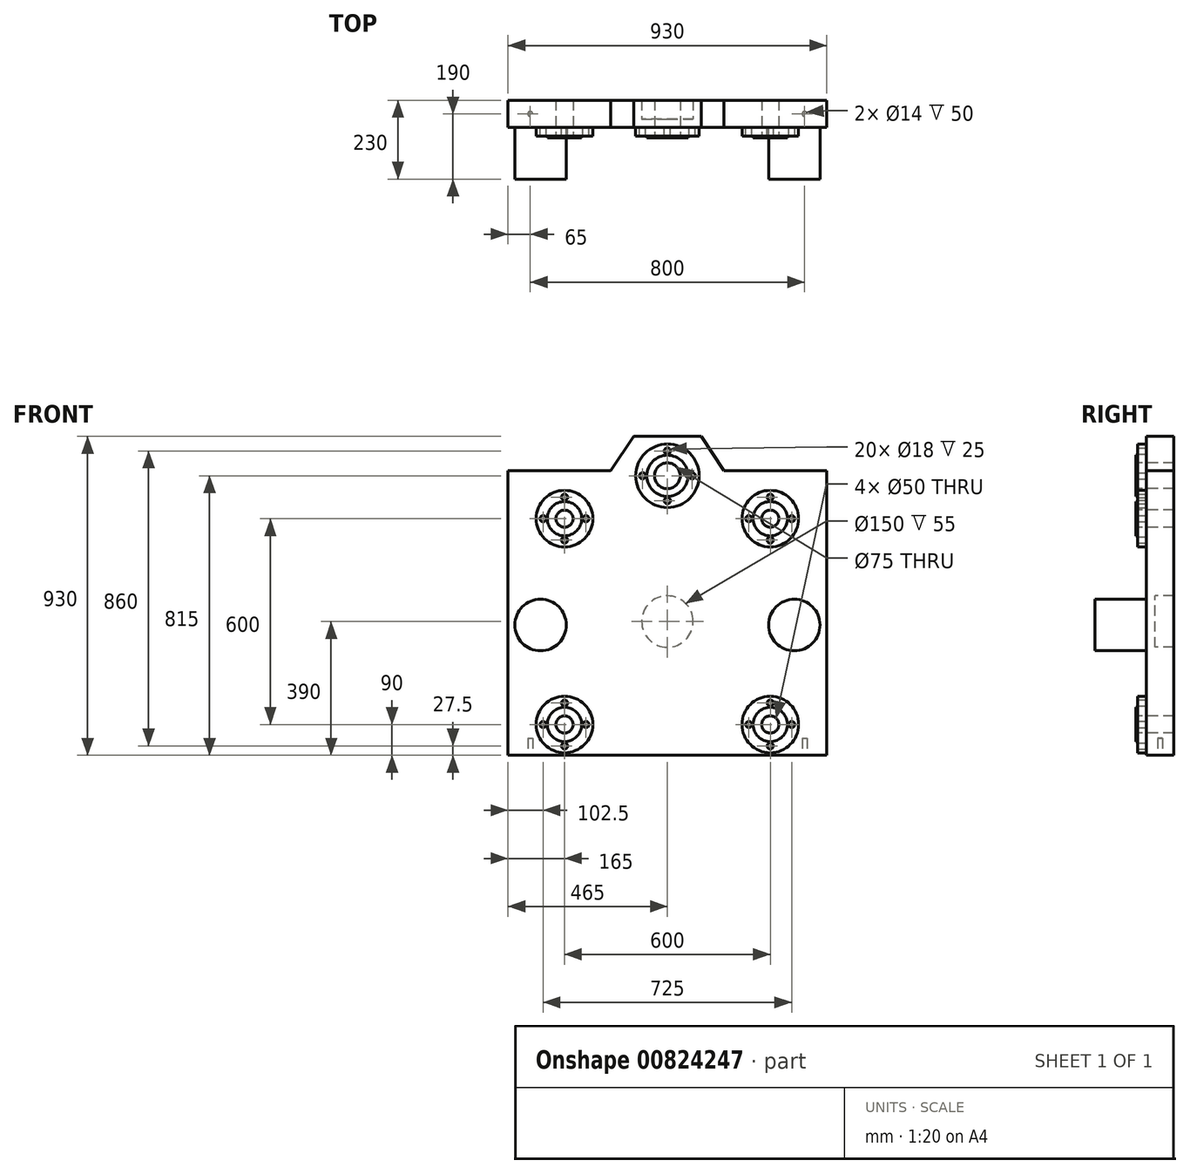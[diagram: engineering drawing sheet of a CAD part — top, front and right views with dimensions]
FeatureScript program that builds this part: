
annotation { "Feature Type Name" : "Feature", "Feature Type Description" : "" }
export const myFeature = defineFeature(function(context is Context, id is Id, definition is map)
    precondition{}
    {
        {
            var Q0;
            Q0=qCreatedBy(makeId("Front.planeOp"),FACE);
            var sketch = newSketch(context, id + "F0", { "sketchPlane" : qUnion([Q0])});
            skLineSegment(sketch, "E0.bottom", {"start": v(465, -965) * mm, "end": v(345, -965) * mm});
            skLineSegment(sketch, "E0.top", {"start": v(465, 965) * mm, "end": v(-465, 965) * mm});
            skLineSegment(sketch, "E0.left", {"start": v(465, -965) * mm, "end": v(465, 965) * mm});
            skLineSegment(sketch, "E0.right", {"start": v(-465, -965) * mm, "end": v(-465, 965) * mm});
            skPoint(sketch, "E0.middle", {"position": v(0, 0) * mm});
            skLineSegment(sketch, "E1.top", {"start": v(-345, -765) * mm, "end": v(345, -765) * mm});
            skLineSegment(sketch, "E1.left", {"start": v(-345, -965) * mm, "end": v(-345, -765) * mm});
            skLineSegment(sketch, "E1.right", {"start": v(345, -965) * mm, "end": v(345, -765) * mm});
            skLineSegment(sketch, "E2.bottom", {"start": v(-345, -645) * mm, "end": v(345, -645) * mm});
            skLineSegment(sketch, "E2.top", {"start": v(-345, -295) * mm, "end": v(345, -295) * mm});
            skLineSegment(sketch, "E2.left", {"start": v(-345, -645) * mm, "end": v(-345, -295) * mm});
            skLineSegment(sketch, "E2.right", {"start": v(345, -645) * mm, "end": v(345, -295) * mm});
            skLineSegment(sketch, "E3.trimOffspring", {"start": v(-345, -965) * mm, "end": v(-465, -965) * mm});
            skLineSegment(sketch, "E4.bottom", {"start": v(-345, -175) * mm, "end": v(345, -175) * mm});
            skLineSegment(sketch, "E4.top", {"start": v(-345, 25) * mm, "end": v(345, 25) * mm});
            skLineSegment(sketch, "E4.left", {"start": v(-345, -175) * mm, "end": v(-345, 25) * mm});
            skLineSegment(sketch, "E4.right", {"start": v(345, -175) * mm, "end": v(345, 25) * mm});
            skPoint(sketch, "E5.middle", {"position": v(0, 425) * mm});
            skSolve(sketch);
        }
        {
            var Q0;
            Q0=makeQuery(id+"F0.imprint","IMPRINT",FACE,{"disambiguationData":[TD([[makeQuery(id+"F0.imprint","IMPRINT",EDGE,{"derivedFrom":sQuery(id+"F0.wireOp",EDGE,"E0.bottom")}),-1.0]])]});
            extrude(context, id + "F1", {"entities" : qUnion([Q0]), "depth" : 80 * mm, "offsetDistance" : 25 * mm});
        }
        {
            var Q0;
            Q0=makeQuery(id+"F1.opExtrude","CAP_FACE",FACE,{"disambiguationData":[OSD([sQuery(id+"F0.wireOp",EDGE,"E0.bottom"),sQuery(id+"F0.wireOp",EDGE,"E0.top"),sQuery(id+"F0.wireOp",EDGE,"E0.left"),sQuery(id+"F0.wireOp",EDGE,"E0.right"),sQuery(id+"F0.wireOp",EDGE,"E1.top"),sQuery(id+"F0.wireOp",EDGE,"E1.left"),sQuery(id+"F0.wireOp",EDGE,"E1.right"),sQuery(id+"F0.wireOp",EDGE,"E2.bottom"),sQuery(id+"F0.wireOp",EDGE,"E2.top"),sQuery(id+"F0.wireOp",EDGE,"E2.left"),sQuery(id+"F0.wireOp",EDGE,"E2.right"),sQuery(id+"F0.wireOp",EDGE,"E3.trimOffspring"),sQuery(id+"F0.wireOp",EDGE,"nSGubIzk-R7de-6MO4-penA-cvBglKJnvsGC"),sQuery(id+"F0.wireOp",EDGE,"E4.bottom"),sQuery(id+"F0.wireOp",EDGE,"E4.top"),sQuery(id+"F0.wireOp",EDGE,"E4.left"),sQuery(id+"F0.wireOp",EDGE,"E4.right")])],"isStart":false});
            var sketch = newSketch(context, id + "F2", { "sketchPlane" : qUnion([Q0])});
            skCircle(sketch, "E6", {"center": v(-300, 125) * mm, "radius": 25 * mm});
            skCircle(sketch, "E7.0", {"center": v(0, 425) * mm, "radius": 75 * mm});
            skCircle(sketch, "E8.0.1.0", {"center": v(-300, 725) * mm, "radius": 25 * mm});
            skCircle(sketch, "E8.1.0.0", {"center": v(300, 125) * mm, "radius": 25 * mm});
            skCircle(sketch, "E8.1.1.0", {"center": v(300, 725) * mm, "radius": 25 * mm});
            skLineSegment(sketch, "E8.direction1", {"start": v(-300, 125) * mm, "end": v(300, 125) * mm, "construction": true});
            skLineSegment(sketch, "E8.direction2", {"start": v(-300, 125) * mm, "end": v(-300, 725) * mm, "construction": true});
            skSolve(sketch);
        }
        {
            var Q0;
            Q0=qSketchRegion(id+"F2",true);
            extrude(context, id + "F3", {"entities" : qUnion([Q0]), "operationType" : NewBodyOperationType.REMOVE, "oppositeDirection" : true, "depth" : 100 * mm, "offsetDistance" : 25 * mm});
        }
        {
            var Q0;
            Q0=makeQuery(id+"F1.opExtrude","CAP_FACE",FACE,{"disambiguationData":[OSD([sQuery(id+"F0.wireOp",EDGE,"E0.bottom"),sQuery(id+"F0.wireOp",EDGE,"E0.top"),sQuery(id+"F0.wireOp",EDGE,"E0.left"),sQuery(id+"F0.wireOp",EDGE,"E0.right"),sQuery(id+"F0.wireOp",EDGE,"E1.top"),sQuery(id+"F0.wireOp",EDGE,"E1.left"),sQuery(id+"F0.wireOp",EDGE,"E1.right"),sQuery(id+"F0.wireOp",EDGE,"E2.bottom"),sQuery(id+"F0.wireOp",EDGE,"E2.top"),sQuery(id+"F0.wireOp",EDGE,"E2.left"),sQuery(id+"F0.wireOp",EDGE,"E2.right"),sQuery(id+"F0.wireOp",EDGE,"E3.trimOffspring"),sQuery(id+"F0.wireOp",EDGE,"nSGubIzk-R7de-6MO4-penA-cvBglKJnvsGC"),sQuery(id+"F0.wireOp",EDGE,"E4.bottom"),sQuery(id+"F0.wireOp",EDGE,"E4.top"),sQuery(id+"F0.wireOp",EDGE,"E4.left"),sQuery(id+"F0.wireOp",EDGE,"E4.right")])],"isStart":false});
            var sketch = newSketch(context, id + "F4", { "sketchPlane" : qUnion([Q0])});
            skCircle(sketch, "E9", {"center": v(-370, 415) * mm, "radius": 75 * mm});
            skCircle(sketch, "E10.MirrorC", {"center": v(370, 415) * mm, "radius": 75 * mm});
            skSolve(sketch);
        }
        {
            var Q0;
            Q0=qSketchRegion(id+"F4",true);
            extrude(context, id + "F5", {"entities" : qUnion([Q0]), "operationType" : NewBodyOperationType.ADD, "depth" : 150 * mm, "offsetDistance" : 25 * mm});
        }
        {
            var Q0;
            Q0=makeQuery(id+"F1.opExtrude","CAP_FACE",FACE,{"disambiguationData":[OSD([sQuery(id+"F0.wireOp",EDGE,"E0.bottom"),sQuery(id+"F0.wireOp",EDGE,"E0.top"),sQuery(id+"F0.wireOp",EDGE,"E0.left"),sQuery(id+"F0.wireOp",EDGE,"E0.right"),sQuery(id+"F0.wireOp",EDGE,"E1.top"),sQuery(id+"F0.wireOp",EDGE,"E1.left"),sQuery(id+"F0.wireOp",EDGE,"E1.right"),sQuery(id+"F0.wireOp",EDGE,"E2.bottom"),sQuery(id+"F0.wireOp",EDGE,"E2.top"),sQuery(id+"F0.wireOp",EDGE,"E2.left"),sQuery(id+"F0.wireOp",EDGE,"E2.right"),sQuery(id+"F0.wireOp",EDGE,"E3.trimOffspring"),sQuery(id+"F0.wireOp",EDGE,"nSGubIzk-R7de-6MO4-penA-cvBglKJnvsGC"),sQuery(id+"F0.wireOp",EDGE,"E4.bottom"),sQuery(id+"F0.wireOp",EDGE,"E4.top"),sQuery(id+"F0.wireOp",EDGE,"E4.left"),sQuery(id+"F0.wireOp",EDGE,"E4.right")])],"isStart":false});
            var sketch = newSketch(context, id + "F6", { "sketchPlane" : qUnion([Q0])});
            skCircle(sketch, "E11", {"center": v(-300, 725) * mm, "radius": 82.5 * mm});
            skCircle(sketch, "E12", {"center": v(-300, 787.5) * mm, "radius": 9 * mm});
            skCircle(sketch, "E13.0", {"center": v(-300, 725) * mm, "radius": 25 * mm});
            skCircle(sketch, "E14.1.0", {"center": v(-362.5, 725) * mm, "radius": 9 * mm});
            skCircle(sketch, "E14.2.0", {"center": v(-300, 662.5) * mm, "radius": 9 * mm});
            skCircle(sketch, "E14.3.0", {"center": v(-237.5, 725) * mm, "radius": 9 * mm});
            skPoint(sketch, "E15.0.1.0", {"position": v(-300, 125) * mm});
            skCircle(sketch, "E15.0.1.1", {"center": v(-300, 125) * mm, "radius": 82.5 * mm});
            skCircle(sketch, "E15.0.1.2", {"center": v(-300, 125) * mm, "radius": 25 * mm});
            skCircle(sketch, "E15.0.1.3", {"center": v(-237.5, 125) * mm, "radius": 9 * mm});
            skCircle(sketch, "E15.0.1.4", {"center": v(-362.5, 125) * mm, "radius": 9 * mm});
            skCircle(sketch, "E15.0.1.5", {"center": v(-300, 187.5) * mm, "radius": 9 * mm});
            skCircle(sketch, "E15.0.1.6", {"center": v(-300, 62.5) * mm, "radius": 9 * mm});
            skPoint(sketch, "E15.1.0.0", {"position": v(300, 725) * mm});
            skCircle(sketch, "E15.1.0.1", {"center": v(300, 725) * mm, "radius": 82.5 * mm});
            skCircle(sketch, "E15.1.0.2", {"center": v(300, 725) * mm, "radius": 25 * mm});
            skCircle(sketch, "E15.1.0.3", {"center": v(362.5, 725) * mm, "radius": 9 * mm});
            skCircle(sketch, "E15.1.0.4", {"center": v(237.5, 725) * mm, "radius": 9 * mm});
            skCircle(sketch, "E15.1.0.5", {"center": v(300, 787.5) * mm, "radius": 9 * mm});
            skCircle(sketch, "E15.1.0.6", {"center": v(300, 662.5) * mm, "radius": 9 * mm});
            skPoint(sketch, "E15.1.1.0", {"position": v(300, 125) * mm});
            skCircle(sketch, "E15.1.1.1", {"center": v(300, 125) * mm, "radius": 82.5 * mm});
            skCircle(sketch, "E15.1.1.2", {"center": v(300, 125) * mm, "radius": 25 * mm});
            skCircle(sketch, "E15.1.1.3", {"center": v(362.5, 125) * mm, "radius": 9 * mm});
            skCircle(sketch, "E15.1.1.4", {"center": v(237.5, 125) * mm, "radius": 9 * mm});
            skCircle(sketch, "E15.1.1.5", {"center": v(300, 187.5) * mm, "radius": 9 * mm});
            skCircle(sketch, "E15.1.1.6", {"center": v(300, 62.5) * mm, "radius": 9 * mm});
            skLineSegment(sketch, "E15.direction1", {"start": v(-300, 662.5) * mm, "end": v(300, 662.5) * mm, "construction": true});
            skLineSegment(sketch, "E15.direction2", {"start": v(-300, 662.5) * mm, "end": v(-300, 62.5) * mm, "construction": true});
            skSolve(sketch);
        }
        {
            var Q0;
            Q0=qSketchRegion(id+"F6",true);
            extrude(context, id + "F7", {"entities" : qUnion([Q0]), "operationType" : NewBodyOperationType.ADD, "depth" : 25 * mm, "offsetDistance" : 25 * mm});
        }
        {
            var Q0;
            Q0=makeQuery(id+"F7.opExtrude","CAP_FACE",FACE,{"disambiguationData":[OSD([sQuery(id+"F6.wireOp",EDGE,"E11"),sQuery(id+"F6.wireOp",EDGE,"E12"),sQuery(id+"F6.wireOp",EDGE,"E13.0"),sQuery(id+"F6.wireOp",EDGE,"E14.1.0"),sQuery(id+"F6.wireOp",EDGE,"E14.2.0"),sQuery(id+"F6.wireOp",EDGE,"E14.3.0")])],"isStart":false});
            var sketch = newSketch(context, id + "F8", { "sketchPlane" : qUnion([Q0])});
            skCircle(sketch, "E16", {"center": v(-300, 725) * mm, "radius": 50 * mm});
            skCircle(sketch, "E17.0.1.0", {"center": v(-300, 125) * mm, "radius": 50 * mm});
            skCircle(sketch, "E17.1.0.0", {"center": v(300, 725) * mm, "radius": 50 * mm});
            skCircle(sketch, "E17.1.1.0", {"center": v(300, 125) * mm, "radius": 50 * mm});
            skLineSegment(sketch, "E17.direction1", {"start": v(-300, 725) * mm, "end": v(300, 725) * mm, "construction": true});
            skLineSegment(sketch, "E17.direction2", {"start": v(-300, 725) * mm, "end": v(-300, 125) * mm, "construction": true});
            skCircle(sketch, "E18", {"center": v(300, 725) * mm, "radius": 25 * mm});
            skCircle(sketch, "E19", {"center": v(300, 125) * mm, "radius": 25 * mm});
            skCircle(sketch, "E20", {"center": v(-300, 125) * mm, "radius": 25 * mm});
            skCircle(sketch, "E21", {"center": v(-300, 725) * mm, "radius": 25 * mm});
            skSolve(sketch);
        }
        {
            var Q0;
            Q0=qSketchRegion(id+"F8",true);
            extrude(context, id + "F9", {"entities" : qUnion([Q0]), "operationType" : NewBodyOperationType.ADD, "depth" : 5 * mm, "offsetDistance" : 25 * mm});
        }
        {
            var Q0;
            {var subQ0=sQuery(id+"F0.wireOp",EDGE,"E4.right");var subQ1=sQuery(id+"F0.wireOp",EDGE,"E4.left");var subQ2=sQuery(id+"F0.wireOp",EDGE,"E4.top");var subQ3=sQuery(id+"F0.wireOp",EDGE,"E1.left");var subQ4=sQuery(id+"F0.wireOp",EDGE,"E4.bottom");var subQ5=sQuery(id+"F0.wireOp",EDGE,"E3.trimOffspring");var subQ6=sQuery(id+"F0.wireOp",EDGE,"E2.right");var subQ7=sQuery(id+"F0.wireOp",EDGE,"E0.left");var subQ8=sQuery(id+"F0.wireOp",EDGE,"E0.top");var subQ9=sQuery(id+"F0.wireOp",EDGE,"E0.right");var subQ10=sQuery(id+"F0.wireOp",EDGE,"E2.bottom");var subQ11=sQuery(id+"F0.wireOp",EDGE,"E0.bottom");var subQ12=sQuery(id+"F0.wireOp",EDGE,"E2.left");var subQ13=sQuery(id+"F0.wireOp",EDGE,"E1.top");var subQ14=sQuery(id+"F0.wireOp",EDGE,"E1.right");var subQ15=sQuery(id+"F0.wireOp",EDGE,"E2.top");Q0=makeQuery(id+"F7.boolean.opBoolean","SPLIT",FACE,{"disambiguationData":[TD([makeQuery(id+"F1.opExtrude","SWEPT_FACE",FACE,{"disambiguationData":[OSD([subQ11])]})])],"derivedFrom":makeQuery(id+"F1.opExtrude","CAP_FACE",FACE,{"disambiguationData":[OSD([subQ11,subQ8,subQ7,subQ9,subQ13,subQ3,subQ14,subQ10,subQ15,subQ12,subQ6,subQ5,subQ4,subQ2,subQ1,subQ0])],"isStart":false})});}
            var sketch = newSketch(context, id + "F10", { "sketchPlane" : qUnion([Q0])});
            skCircle(sketch, "E22.0", {"center": v(0, 425) * mm, "radius": 75 * mm});
            skSolve(sketch);
        }
        {
            var Q0;
            Q0=qSketchRegion(id+"F10",true);
            extrude(context, id + "F11", {"entities" : qUnion([Q0]), "operationType" : NewBodyOperationType.ADD, "oppositeDirection" : true, "depth" : 25 * mm, "offsetDistance" : 25 * mm});
        }
        {
            var Q0;
            {var subQ0=sQuery(id+"F0.wireOp",EDGE,"E4.right");var subQ1=sQuery(id+"F0.wireOp",EDGE,"E4.left");var subQ2=sQuery(id+"F0.wireOp",EDGE,"E4.top");var subQ3=sQuery(id+"F0.wireOp",EDGE,"E1.left");var subQ4=sQuery(id+"F0.wireOp",EDGE,"E4.bottom");var subQ5=sQuery(id+"F0.wireOp",EDGE,"E3.trimOffspring");var subQ6=sQuery(id+"F0.wireOp",EDGE,"E2.right");var subQ7=sQuery(id+"F0.wireOp",EDGE,"E0.left");var subQ8=sQuery(id+"F0.wireOp",EDGE,"E0.top");var subQ9=sQuery(id+"F0.wireOp",EDGE,"E0.right");var subQ10=sQuery(id+"F0.wireOp",EDGE,"E2.bottom");var subQ11=sQuery(id+"F0.wireOp",EDGE,"E0.bottom");var subQ12=sQuery(id+"F0.wireOp",EDGE,"E2.left");var subQ13=sQuery(id+"F0.wireOp",EDGE,"E1.top");var subQ14=sQuery(id+"F0.wireOp",EDGE,"E1.right");var subQ15=sQuery(id+"F0.wireOp",EDGE,"E2.top");Q0=makeQuery(id+"F11.boolean.opBoolean","MERGE",FACE,{"derivedFrom":[makeQuery(id+"F7.boolean.opBoolean","SPLIT",FACE,{"disambiguationData":[TD([makeQuery(id+"F1.opExtrude","SWEPT_FACE",FACE,{"disambiguationData":[OSD([subQ11])]})])],"derivedFrom":makeQuery(id+"F1.opExtrude","CAP_FACE",FACE,{"disambiguationData":[OSD([subQ11,subQ8,subQ7,subQ9,subQ13,subQ3,subQ14,subQ10,subQ15,subQ12,subQ6,subQ5,subQ4,subQ2,subQ1,subQ0])],"isStart":false})}),makeQuery(id+"F11.opExtrude","CAP_FACE",FACE,{"disambiguationData":[OSD([sQuery(id+"F10.wireOp",EDGE,"E22.0")])],"isStart":true})]});}
            var sketch = newSketch(context, id + "F12", { "sketchPlane" : qUnion([Q0])});
            skCircle(sketch, "E23", {"center": v(0, 850) * mm, "radius": 37.5 * mm});
            skPoint(sketch, "E23.centerSnap0", {"position": v(0, 965) * mm});
            skCircle(sketch, "E24.0", {"center": v(300, 725) * mm, "radius": 25 * mm});
            skSolve(sketch);
        }
        {
            var Q0;
            Q0=makeQuery(id+"F12.imprint","IMPRINT",FACE,{"disambiguationData":[TD([[makeQuery(id+"F12.imprint","IMPRINT",EDGE,{"derivedFrom":sQuery(id+"F12.wireOp",EDGE,"E23")}),1.0]])]});
            extrude(context, id + "F13", {"entities" : qUnion([Q0]), "operationType" : NewBodyOperationType.REMOVE, "oppositeDirection" : true, "depth" : 100 * mm, "offsetDistance" : 25 * mm});
        }
        {
            var Q0;
            {var subQ0=sQuery(id+"F0.wireOp",EDGE,"E4.right");var subQ1=sQuery(id+"F0.wireOp",EDGE,"E4.left");var subQ2=sQuery(id+"F0.wireOp",EDGE,"E4.top");var subQ3=sQuery(id+"F0.wireOp",EDGE,"E1.left");var subQ4=sQuery(id+"F0.wireOp",EDGE,"E4.bottom");var subQ5=sQuery(id+"F0.wireOp",EDGE,"E3.trimOffspring");var subQ6=sQuery(id+"F0.wireOp",EDGE,"E2.right");var subQ7=sQuery(id+"F0.wireOp",EDGE,"E0.left");var subQ8=sQuery(id+"F0.wireOp",EDGE,"E0.top");var subQ9=sQuery(id+"F0.wireOp",EDGE,"E0.right");var subQ10=sQuery(id+"F0.wireOp",EDGE,"E2.bottom");var subQ11=sQuery(id+"F0.wireOp",EDGE,"E0.bottom");var subQ12=sQuery(id+"F0.wireOp",EDGE,"E2.left");var subQ13=sQuery(id+"F0.wireOp",EDGE,"E1.top");var subQ14=sQuery(id+"F0.wireOp",EDGE,"E1.right");var subQ15=sQuery(id+"F0.wireOp",EDGE,"E2.top");Q0=makeQuery(id+"F11.boolean.opBoolean","MERGE",FACE,{"derivedFrom":[makeQuery(id+"F7.boolean.opBoolean","SPLIT",FACE,{"disambiguationData":[TD([makeQuery(id+"F1.opExtrude","SWEPT_FACE",FACE,{"disambiguationData":[OSD([subQ11])]})])],"derivedFrom":makeQuery(id+"F1.opExtrude","CAP_FACE",FACE,{"disambiguationData":[OSD([subQ11,subQ8,subQ7,subQ9,subQ13,subQ3,subQ14,subQ10,subQ15,subQ12,subQ6,subQ5,subQ4,subQ2,subQ1,subQ0])],"isStart":false})}),makeQuery(id+"F11.opExtrude","CAP_FACE",FACE,{"disambiguationData":[OSD([sQuery(id+"F10.wireOp",EDGE,"E22.0")])],"isStart":true})]});}
            var sketch = newSketch(context, id + "F14", { "sketchPlane" : qUnion([Q0])});
            skCircle(sketch, "E25", {"center": v(0, 850) * mm, "radius": 92.5 * mm});
            skCircle(sketch, "E26", {"center": v(0, 922.5) * mm, "radius": 9 * mm});
            skCircle(sketch, "E27.1.0", {"center": v(-72.5, 850) * mm, "radius": 9 * mm});
            skCircle(sketch, "E27.2.0", {"center": v(0, 777.5) * mm, "radius": 9 * mm});
            skCircle(sketch, "E27.3.0", {"center": v(72.5, 850) * mm, "radius": 9 * mm});
            skSolve(sketch);
        }
        {
            var Q0;
            Q0=makeQuery(id+"F14.imprint","IMPRINT",FACE,{"disambiguationData":[TD([[makeQuery(id+"F14.imprint","IMPRINT",EDGE,{"derivedFrom":sQuery(id+"F14.wireOp",EDGE,"E25")}),1.0]])]});
            extrude(context, id + "F15", {"entities" : qUnion([Q0]), "operationType" : NewBodyOperationType.ADD, "depth" : 25 * mm, "offsetDistance" : 25 * mm});
        }
        {
            var Q0;
            Q0=makeQuery(id+"F15.opExtrude","CAP_FACE",FACE,{"disambiguationData":[OSD([sQuery(id+"F12.wireOp",EDGE,"E23"),sQuery(id+"F14.wireOp",EDGE,"E25"),sQuery(id+"F14.wireOp",EDGE,"E26"),sQuery(id+"F14.wireOp",EDGE,"E27.1.0"),sQuery(id+"F14.wireOp",EDGE,"E27.2.0"),sQuery(id+"F14.wireOp",EDGE,"E27.3.0")])],"isStart":false});
            var sketch = newSketch(context, id + "F16", { "sketchPlane" : qUnion([Q0])});
            skCircle(sketch, "E28", {"center": v(0, 850) * mm, "radius": 60 * mm});
            skSolve(sketch);
        }
        {
            var Q0;
            Q0=makeQuery(id+"F16.imprint","IMPRINT",FACE,{"disambiguationData":[TD([[makeQuery(id+"F16.imprint","IMPRINT",EDGE,{"derivedFrom":sQuery(id+"F16.wireOp",EDGE,"E28")}),1.0]])]});
            extrude(context, id + "F17", {"entities" : qUnion([Q0]), "operationType" : NewBodyOperationType.ADD, "depth" : 5 * mm, "offsetDistance" : 25 * mm});
        }
        {
            var Q0;
            {var subQ2=sQuery(id+"F0.wireOp",EDGE,"E4.right");var subQ5=sQuery(id+"F0.wireOp",EDGE,"E4.left");var subQ8=sQuery(id+"F0.wireOp",EDGE,"E4.top");var subQ10=sQuery(id+"F0.wireOp",EDGE,"E4.bottom");var subQ12=sQuery(id+"F0.wireOp",EDGE,"E3.trimOffspring");var subQ14=sQuery(id+"F0.wireOp",EDGE,"E2.right");var subQ16=sQuery(id+"F0.wireOp",EDGE,"E0.left");var subQ18=sQuery(id+"F0.wireOp",EDGE,"E0.top");var subQ20=sQuery(id+"F0.wireOp",EDGE,"E0.right");var subQ23=sQuery(id+"F0.wireOp",EDGE,"E2.bottom");var subQ25=sQuery(id+"F0.wireOp",EDGE,"E0.bottom");var subQ26=makeQuery(id+"F1.opExtrude","SWEPT_FACE",FACE,{"disambiguationData":[OSD([subQ25])]});var subQ27=sQuery(id+"F0.wireOp",EDGE,"E2.left");var subQ29=sQuery(id+"F0.wireOp",EDGE,"E1.top");var subQ32=sQuery(id+"F0.wireOp",EDGE,"E1.left");var subQ34=sQuery(id+"F0.wireOp",EDGE,"E1.right");var subQ36=sQuery(id+"F0.wireOp",EDGE,"E2.top");Q0=makeQuery(id+"F15.boolean.opBoolean","SPLIT",FACE,{"disambiguationData":[TD([subQ26])],"derivedFrom":makeQuery(id+"F11.boolean.opBoolean","MERGE",FACE,{"derivedFrom":[makeQuery(id+"F7.boolean.opBoolean","SPLIT",FACE,{"disambiguationData":[TD([subQ26])],"derivedFrom":makeQuery(id+"F1.opExtrude","CAP_FACE",FACE,{"disambiguationData":[OSD([subQ25,subQ18,subQ16,subQ20,subQ29,subQ32,subQ34,subQ23,subQ36,subQ27,subQ14,subQ12,subQ10,subQ8,subQ5,subQ2])],"isStart":false})}),makeQuery(id+"F11.opExtrude","CAP_FACE",FACE,{"disambiguationData":[OSD([sQuery(id+"F10.wireOp",EDGE,"E22.0")])],"isStart":true})]})});}
            var sketch = newSketch(context, id + "F18", { "sketchPlane" : qUnion([Q0])});
            skLineSegment(sketch, "E29.bottom", {"start": v(-465, -965) * mm, "end": v(465, -965) * mm});
            skLineSegment(sketch, "E29.top", {"start": v(-465, 35) * mm, "end": v(465, 35) * mm});
            skLineSegment(sketch, "E29.left", {"start": v(-465, -965) * mm, "end": v(-465, 35) * mm});
            skLineSegment(sketch, "E29.right", {"start": v(465, -965) * mm, "end": v(465, 35) * mm});
            skSolve(sketch);
        }
        {
            var Q0;
            Q0 = qSketchRegion(id + "F18", true);
            extrude(context, id + "F19", {"entities" : qUnion([Q0]), "operationType" : NewBodyOperationType.REMOVE, "oppositeDirection" : true, "depth" : 100 * mm, "offsetDistance" : 25 * mm});
        }
        {
            var Q0;
            Q0=makeQuery(id+"F19.boolean.opBoolean","COPY",FACE,{"derivedFrom":makeQuery(id+"F19.opExtrude","SWEPT_FACE",FACE,{"disambiguationData":[OSD([sQuery(id+"F18.wireOp",EDGE,"E29.top")])]})});
            var sketch = newSketch(context, id + "F20", { "sketchPlane" : qUnion([Q0])});
            skCircle(sketch, "E30", {"center": v(-400, 40) * mm, "radius": 7 * mm});
            skCircle(sketch, "E31.MirrorC", {"center": v(400, 40) * mm, "radius": 7 * mm});
            skSolve(sketch);
        }
        {
            var Q0;
            Q0 = qSketchRegion(id + "F20", true);
            extrude(context, id + "F21", {"entities" : qUnion([Q0]), "operationType" : NewBodyOperationType.REMOVE, "oppositeDirection" : true, "depth" : 50 * mm, "offsetDistance" : 25 * mm});
        }
        {
            var Q0;
            {var subQ2=sQuery(id+"F0.wireOp",EDGE,"E4.right");var subQ5=sQuery(id+"F0.wireOp",EDGE,"E4.left");var subQ8=sQuery(id+"F0.wireOp",EDGE,"E4.top");var subQ10=sQuery(id+"F0.wireOp",EDGE,"E4.bottom");var subQ12=sQuery(id+"F0.wireOp",EDGE,"E3.trimOffspring");var subQ14=sQuery(id+"F0.wireOp",EDGE,"E2.right");var subQ16=sQuery(id+"F0.wireOp",EDGE,"E0.left");var subQ18=sQuery(id+"F0.wireOp",EDGE,"E0.top");var subQ20=sQuery(id+"F0.wireOp",EDGE,"E0.right");var subQ23=sQuery(id+"F0.wireOp",EDGE,"E2.bottom");var subQ25=sQuery(id+"F0.wireOp",EDGE,"E0.bottom");var subQ26=makeQuery(id+"F1.opExtrude","SWEPT_FACE",FACE,{"disambiguationData":[OSD([subQ25])]});var subQ27=sQuery(id+"F0.wireOp",EDGE,"E2.left");var subQ29=sQuery(id+"F0.wireOp",EDGE,"E1.top");var subQ32=sQuery(id+"F0.wireOp",EDGE,"E1.left");var subQ34=sQuery(id+"F0.wireOp",EDGE,"E1.right");var subQ36=sQuery(id+"F0.wireOp",EDGE,"E2.top");Q0=makeQuery(id+"F15.boolean.opBoolean","SPLIT",FACE,{"disambiguationData":[TD([subQ26])],"derivedFrom":makeQuery(id+"F11.boolean.opBoolean","MERGE",FACE,{"derivedFrom":[makeQuery(id+"F7.boolean.opBoolean","SPLIT",FACE,{"disambiguationData":[TD([subQ26])],"derivedFrom":makeQuery(id+"F1.opExtrude","CAP_FACE",FACE,{"disambiguationData":[OSD([subQ25,subQ18,subQ16,subQ20,subQ29,subQ32,subQ34,subQ23,subQ36,subQ27,subQ14,subQ12,subQ10,subQ8,subQ5,subQ2])],"isStart":false})}),makeQuery(id+"F11.opExtrude","CAP_FACE",FACE,{"disambiguationData":[OSD([sQuery(id+"F10.wireOp",EDGE,"E22.0")])],"isStart":true})]})});}
            var sketch = newSketch(context, id + "F22", { "sketchPlane" : qUnion([Q0])});
            skLineSegment(sketch, "E32.bottom", {"start": v(-465, 965) * mm, "end": v(-165, 965) * mm});
            skLineSegment(sketch, "E32.top", {"start": v(-465, 865) * mm, "end": v(-165, 865) * mm});
            skLineSegment(sketch, "E32.left", {"start": v(-465, 965) * mm, "end": v(-465, 865) * mm});
            skLineSegment(sketch, "E32.right", {"start": v(-165, 965) * mm, "end": v(-165, 865) * mm});
            skLineSegment(sketch, "E33.bottom", {"start": v(465, 965) * mm, "end": v(165, 965) * mm});
            skLineSegment(sketch, "E33.top", {"start": v(465, 865) * mm, "end": v(165, 865) * mm});
            skLineSegment(sketch, "E33.left", {"start": v(465, 965) * mm, "end": v(465, 865) * mm});
            skLineSegment(sketch, "E33.right", {"start": v(165, 965) * mm, "end": v(165, 865) * mm});
            skLineSegment(sketch, "E34", {"start": v(165, 865) * mm, "end": v(98.67, 965) * mm});
            skLineSegment(sketch, "E35", {"start": v(-165, 865) * mm, "end": v(-98.67, 965) * mm});
            skLineSegment(sketch, "E36", {"start": v(-98.67, 965) * mm, "end": v(-165, 965) * mm});
            skLineSegment(sketch, "E37", {"start": v(98.67, 965) * mm, "end": v(165, 965) * mm});
            skSolve(sketch);
        }
        {
            var Q0;
            Q0 = qSketchRegion(id + "F22", true);
            extrude(context, id + "F23", {"entities" : qUnion([Q0]), "operationType" : NewBodyOperationType.REMOVE, "oppositeDirection" : true, "depth" : 80 * mm, "offsetDistance" : 25 * mm});
        }
    });
